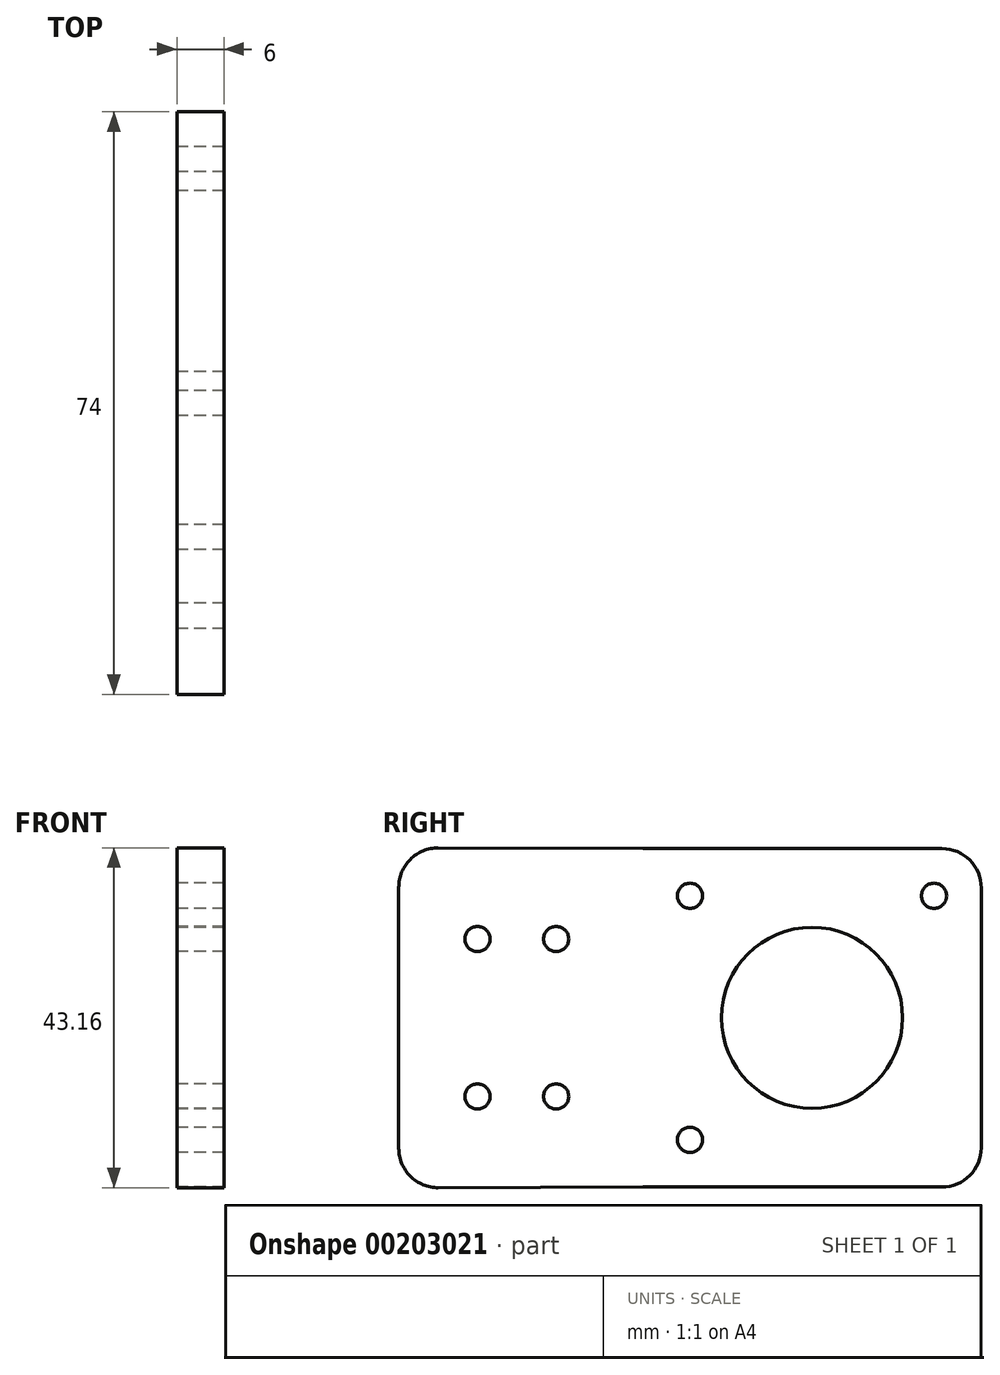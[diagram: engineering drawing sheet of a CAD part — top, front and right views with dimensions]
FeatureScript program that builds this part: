
annotation { "Feature Type Name" : "Feature", "Feature Type Description" : "" }
export const myFeature = defineFeature(function(context is Context, id is Id, definition is map)
    precondition{}
    {
        {
            var Q0;
            Q0=qCreatedBy(makeId("Right.planeOp"),FACE);
            var sketch = newSketch(context, id + "F0", { "sketchPlane" : qUnion([Q0])});
            skCircle(sketch, "E0", {"center": v(68.5, -15.5) * mm, "radius": 1.6 * mm});
            skCircle(sketch, "E1", {"center": v(68.5, 15.5) * mm, "radius": 1.6 * mm});
            skCircle(sketch, "E2", {"center": v(37.5, 15.5) * mm, "radius": 1.6 * mm});
            skCircle(sketch, "E3", {"center": v(37.5, -15.5) * mm, "radius": 1.6 * mm});
            skCircle(sketch, "E4", {"center": v(53, 0) * mm, "radius": 11.5 * mm});
            skLineSegment(sketch, "E5", {"start": v(69.5, -21.5) * mm, "end": v(31.5, -21.5) * mm});
            skArc(sketch, "E6", {"start": v(31.5, -21.5) * mm, "mid": v(31.5, -21.5) * mm, "end": v(31.5, -21.5) * mm});
            skLineSegment(sketch, "E7", {"start": v(31.5, -21.5) * mm, "end": v(5.52, -21.58) * mm});
            skArc(sketch, "E8", {"start": v(5.52, -21.58) * mm, "mid": v(1.97, -20.13) * mm, "end": v(0.5, -16.58) * mm});
            skLineSegment(sketch, "E9", {"start": v(0.5, -16.58) * mm, "end": v(0.5, 16.58) * mm});
            skArc(sketch, "E10", {"start": v(0.5, 16.58) * mm, "mid": v(1.97, 20.13) * mm, "end": v(5.52, 21.58) * mm});
            skLineSegment(sketch, "E11", {"start": v(5.52, 21.58) * mm, "end": v(31.5, 21.5) * mm});
            skArc(sketch, "E12", {"start": v(31.5, 21.5) * mm, "mid": v(31.5, 21.5) * mm, "end": v(31.5, 21.5) * mm});
            skLineSegment(sketch, "E13", {"start": v(31.5, 21.5) * mm, "end": v(69.5, 21.5) * mm});
            skArc(sketch, "E14", {"start": v(69.5, 21.5) * mm, "mid": v(73.04, 20.04) * mm, "end": v(74.5, 16.5) * mm});
            skLineSegment(sketch, "E15", {"start": v(74.5, 16.5) * mm, "end": v(74.5, -16.5) * mm});
            skArc(sketch, "E16", {"start": v(74.5, -16.5) * mm, "mid": v(73.04, -20.04) * mm, "end": v(69.5, -21.5) * mm});
            skCircle(sketch, "E17", {"center": v(20.5, 10) * mm, "radius": 1.6 * mm});
            skCircle(sketch, "E18", {"center": v(20.5, -10) * mm, "radius": 1.6 * mm});
            skCircle(sketch, "E19", {"center": v(10.5, -10) * mm, "radius": 1.6 * mm});
            skCircle(sketch, "E20", {"center": v(10.5, 10) * mm, "radius": 1.6 * mm});
            skSolve(sketch);
        }
        {
            var Q0;
            Q0 = qSketchRegion(id + "F0", true);
            var Q1;
            Q1=makeQuery(id+"F0.imprint","IMPRINT",FACE,{"disambiguationData":[TD([[makeQuery(id+"F0.imprint","IMPRINT",EDGE,{"derivedFrom":sQuery(id+"F0.wireOp",EDGE,"E0")}),1.0]])]});
            extrude(context, id + "F1", {"entities" : qUnion([Q0, Q1]), "depth" : 6 * mm});
        }
    });
